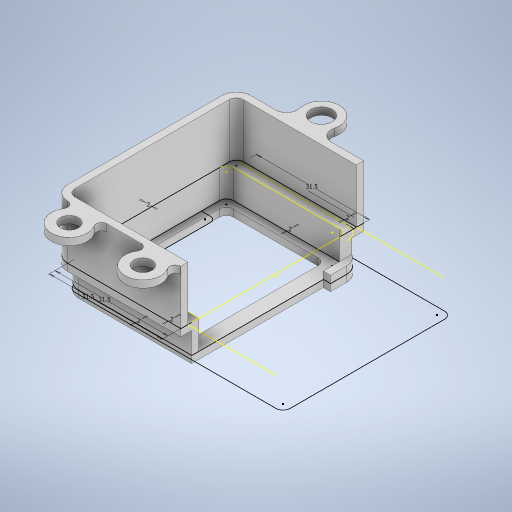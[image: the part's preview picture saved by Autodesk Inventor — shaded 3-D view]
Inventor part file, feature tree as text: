
AUTODESK INVENTOR PART (.ipt)
format: ipt  version: 2023 (Build 270158000, 158)  size: 453,120 bytes
history: native  units: in
note: dims shown in document units (in); Inventor stores cm internally (conversion verified against a paired STEP export)
features: extrude x7, sketch x6, projected_geometry x3, plane x1
ambient origin geometry x8: Origin, YZ Plane, XZ Plane, XY Plane, X Axis, Y Axis, Z Axis, Center Point
bodies: Body1 (feature_tree)
feature tree (17):
  sketch  "Sketch1"  dims[d8=0.0787in d9=0.0787in]
  extrude  "Extrusion3"  Depth=0.0787in
  plane  "Work Plane1"
  extrude  "Extrusion4"  Depth=0.315in TaperAngle=0.0deg
  sketch  "Sketch2"  dims[d10=0.0787in d11=0.0in d12=0.315in d13=0.0in]
  sketch  "Sketch3"  dims[d14=0.315in d18=0.0787in]
  extrude  "Extrusion7"  Depth=0.0787in
  extrude  "Extrusion8"  Depth=0.0787in
  extrude  "Extrusion9"  Depth=1.2402in
  extrude  "Extrusion10"  Depth=0.0787in TaperAngle=0.0deg
  extrude  "Extrusion11"  Depth=0.5906in TaperAngle=0.0deg
  projected_geometry  "Projected Loop1"
  projected_geometry  "Projected Loop2"
  sketch  "Sketch4"  dims[d19=0.0787in d20=0.0787in]
  sketch  "Sketch5"  dims[d21=1.2402in d22=1.2402in]
  sketch  "Sketch6"  dims[d23=1.2402in d28=0.0787in d29=0.0in d30=0.5906in d31=0.0in d32=0.2362in d33=0.0in d34=0.3937in d35=0.2362in d36=1.3189in d37=0.6594in d38=0.1181in d39=0.1181in d40=0.3937in d41=0.1969in d42=0.1181in d43=0.1181in d44=0.3937in d45=0.1969in d46=0.1181in d47=0.1181in d49=0.8071in d50=0.0787in d51=0.0in d52=0.1575in d53=1.4646in d54=1.0827in d55=0.1575in d56=0.0787in d57=0.0787in d58=0.0in]
  projected_geometry  "Projected Loop3"
